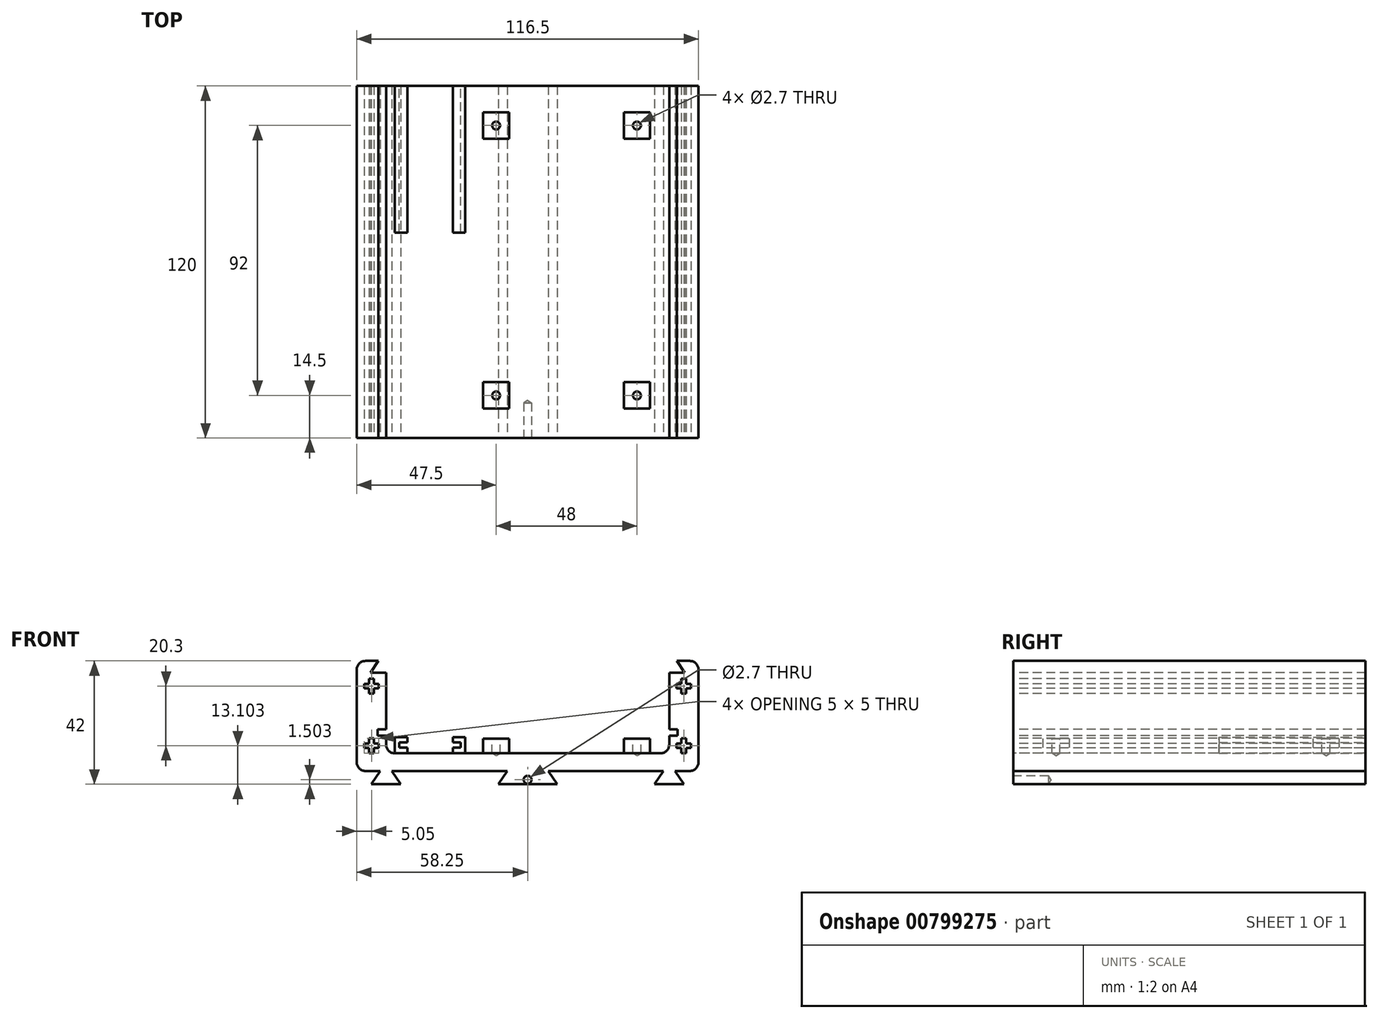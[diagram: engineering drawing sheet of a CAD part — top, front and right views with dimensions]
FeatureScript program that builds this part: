
annotation { "Feature Type Name" : "Feature", "Feature Type Description" : "" }
export const myFeature = defineFeature(function(context is Context, id is Id, definition is map)
    precondition{}
    {
        {
            var Q0;
            Q0=qCreatedBy(makeId("Front.planeOp"),FACE);
            var sketch = newSketch(context, id + "F0", { "sketchPlane" : qUnion([Q0])});
            skLineSegment(sketch, "E0", {"start": v(0, -17) * mm, "end": v(-10.04, -17) * mm});
            skLineSegment(sketch, "E1", {"start": v(-10.04, -17) * mm, "end": v(-7, -12.5) * mm});
            skLineSegment(sketch, "E2", {"start": v(-7, -12.5) * mm, "end": v(-46.25, -12.5) * mm});
            skLineSegment(sketch, "E3", {"start": v(-46.25, -12.5) * mm, "end": v(-43.21, -17) * mm});
            skLineSegment(sketch, "E4", {"start": v(-43.21, -17) * mm, "end": v(-53.29, -17) * mm});
            skLineSegment(sketch, "E5", {"start": v(-53.29, -17) * mm, "end": v(-50.25, -12.5) * mm});
            skLineSegment(sketch, "E6", {"start": v(-50.25, -12.5) * mm, "end": v(-55.25, -12.5) * mm});
            skLineSegment(sketch, "E7", {"start": v(-58.25, -9.5) * mm, "end": v(-58.25, 22) * mm});
            skLineSegment(sketch, "E8", {"start": v(-55.25, 25) * mm, "end": v(-50.87, 25) * mm});
            skLineSegment(sketch, "E9", {"start": v(-50.87, 25) * mm, "end": v(-53.5, 21) * mm});
            skLineSegment(sketch, "E10", {"start": v(-53.5, 21) * mm, "end": v(-48.25, 21) * mm});
            skLineSegment(sketch, "E11", {"start": v(-48.25, 21) * mm, "end": v(-48.25, 1.7) * mm});
            skLineSegment(sketch, "E12", {"start": v(-48.25, 1.7) * mm, "end": v(-51.1, 1.7) * mm});
            skLineSegment(sketch, "E13", {"start": v(-51.1, 1.7) * mm, "end": v(-51.1, -0.5) * mm});
            skLineSegment(sketch, "E14", {"start": v(-51.1, -0.5) * mm, "end": v(-48.25, -0.5) * mm});
            skLineSegment(sketch, "E15", {"start": v(-48.25, -0.5) * mm, "end": v(-48.25, -3.5) * mm});
            skLineSegment(sketch, "E16", {"start": v(-45.25, -6.5) * mm, "end": v(0, -6.5) * mm});
            skLineSegment(sketch, "E17", {"start": v(-48.25, 29.47) * mm, "end": v(-48.25, -26.87) * mm, "construction": true});
            skPoint(sketch, "E18.visualSharp", {"position": v(-58.25, 25) * mm});
            skArc(sketch, "E18.filletArc", {"start": v(-55.25, 25) * mm, "mid": v(-57.37, 24.11) * mm, "end": v(-58.25, 22) * mm});
            skPoint(sketch, "E19.visualSharp", {"position": v(-58.25, -12.5) * mm});
            skArc(sketch, "E19.filletArc", {"start": v(-58.25, -9.5) * mm, "mid": v(-57.37, -11.63) * mm, "end": v(-55.25, -12.5) * mm});
            skPoint(sketch, "E20.visualSharp", {"position": v(-48.25, -6.5) * mm});
            skArc(sketch, "E20.filletArc", {"start": v(-48.25, -3.5) * mm, "mid": v(-47.37, -5.63) * mm, "end": v(-45.25, -6.5) * mm});
            skLineSegment(sketch, "E21", {"start": v(-53.2, 35.2) * mm, "end": v(-53.2, -9.28) * mm, "construction": true});
            skLineSegment(sketch, "E22", {"start": v(-92.18, 6.24) * mm, "end": v(0, 6.24) * mm, "construction": true});
            skArc(sketch, "E23.MirrorCS", {"start": v(48.25, -3.5) * mm, "mid": v(47.37, -5.63) * mm, "end": v(45.25, -6.5) * mm});
            skArc(sketch, "E24.MirrorCS", {"start": v(55.25, 25) * mm, "mid": v(57.37, 24.11) * mm, "end": v(58.25, 22) * mm});
            skLineSegment(sketch, "E25.MirrorCS", {"start": v(48.25, -0.5) * mm, "end": v(48.25, -3.5) * mm});
            skLineSegment(sketch, "E26.MirrorCS", {"start": v(46.25, -12.5) * mm, "end": v(43.21, -17) * mm});
            skLineSegment(sketch, "E27.MirrorCS", {"start": v(51.1, 1.7) * mm, "end": v(51.1, -0.5) * mm});
            skLineSegment(sketch, "E28.MirrorCS", {"start": v(53.29, -17) * mm, "end": v(50.25, -12.5) * mm});
            skLineSegment(sketch, "E29.MirrorCS", {"start": v(10.04, -17) * mm, "end": v(7, -12.5) * mm});
            skLineSegment(sketch, "E30.MirrorCS", {"start": v(48.25, 1.7) * mm, "end": v(51.1, 1.7) * mm});
            skLineSegment(sketch, "E31.MirrorCS", {"start": v(51.1, -0.5) * mm, "end": v(48.25, -0.5) * mm});
            skArc(sketch, "E32.MirrorCS", {"start": v(58.25, -9.5) * mm, "mid": v(57.37, -11.63) * mm, "end": v(55.25, -12.5) * mm});
            skLineSegment(sketch, "E33.MirrorCS", {"start": v(45.25, -6.5) * mm, "end": v(0, -6.5) * mm});
            skLineSegment(sketch, "E34.MirrorCS", {"start": v(48.25, 29.47) * mm, "end": v(48.25, -26.87) * mm, "construction": true});
            skLineSegment(sketch, "E35.MirrorCS", {"start": v(0, -17) * mm, "end": v(10.04, -17) * mm});
            skPoint(sketch, "E36.MirrorP", {"position": v(58.25, -12.5) * mm});
            skLineSegment(sketch, "E37.MirrorCS", {"start": v(7, -12.5) * mm, "end": v(46.25, -12.5) * mm});
            skLineSegment(sketch, "E38.MirrorCS", {"start": v(43.21, -17) * mm, "end": v(53.29, -17) * mm});
            skPoint(sketch, "E39.MirrorP", {"position": v(58.25, 25) * mm});
            skLineSegment(sketch, "E40.MirrorCS", {"start": v(50.25, -12.5) * mm, "end": v(55.25, -12.5) * mm});
            skLineSegment(sketch, "E41.MirrorCS", {"start": v(53.2, 35.2) * mm, "end": v(53.2, -9.28) * mm, "construction": true});
            skPoint(sketch, "E42.MirrorP", {"position": v(48.25, -6.5) * mm});
            skLineSegment(sketch, "E43.MirrorCS", {"start": v(58.25, -9.5) * mm, "end": v(58.25, 22) * mm});
            skLineSegment(sketch, "E44.MirrorCS", {"start": v(53.5, 21) * mm, "end": v(48.25, 21) * mm});
            skLineSegment(sketch, "E45.MirrorCS", {"start": v(48.25, 21) * mm, "end": v(48.25, 1.7) * mm});
            skLineSegment(sketch, "E46.MirrorCS", {"start": v(55.25, 25) * mm, "end": v(50.87, 25) * mm});
            skLineSegment(sketch, "E47.MirrorCS", {"start": v(50.87, 25) * mm, "end": v(53.5, 21) * mm});
            skPoint(sketch, "E48", {"position": v(-53.2, 16.4) * mm});
            skPoint(sketch, "E49", {"position": v(-53.2, -3.9) * mm});
            skLineSegment(sketch, "E50", {"start": v(-55.7, 17.2) * mm, "end": v(-54, 17.2) * mm});
            skLineSegment(sketch, "E51", {"start": v(-54, 17.2) * mm, "end": v(-54, 18.9) * mm});
            skLineSegment(sketch, "E52", {"start": v(-54, 18.9) * mm, "end": v(-52.4, 18.9) * mm});
            skLineSegment(sketch, "E53", {"start": v(-52.4, 18.9) * mm, "end": v(-52.4, 17.2) * mm});
            skLineSegment(sketch, "E54", {"start": v(-52.4, 17.2) * mm, "end": v(-50.7, 17.2) * mm});
            skLineSegment(sketch, "E55", {"start": v(-50.7, 17.2) * mm, "end": v(-50.7, 15.6) * mm});
            skLineSegment(sketch, "E56", {"start": v(-50.7, 15.6) * mm, "end": v(-52.4, 15.6) * mm});
            skLineSegment(sketch, "E57", {"start": v(-52.4, 15.6) * mm, "end": v(-52.4, 13.9) * mm});
            skLineSegment(sketch, "E58", {"start": v(-52.4, 13.9) * mm, "end": v(-54, 13.9) * mm});
            skLineSegment(sketch, "E59", {"start": v(-54, 13.9) * mm, "end": v(-54, 15.6) * mm});
            skLineSegment(sketch, "E60", {"start": v(-54, 15.6) * mm, "end": v(-55.7, 15.6) * mm});
            skLineSegment(sketch, "E61", {"start": v(-55.7, 15.6) * mm, "end": v(-55.7, 17.2) * mm});
            skLineSegment(sketch, "E62", {"start": v(-50.4, 16.4) * mm, "end": v(-59.4, 16.4) * mm, "construction": true});
            skLineSegment(sketch, "E63", {"start": v(-49.34, -3.9) * mm, "end": v(-57.36, -3.9) * mm, "construction": true});
            skLineSegment(sketch, "E64", {"start": v(-54, -1.4) * mm, "end": v(-52.4, -1.4) * mm});
            skLineSegment(sketch, "E65", {"start": v(-52.4, -1.4) * mm, "end": v(-52.4, -3.1) * mm});
            skLineSegment(sketch, "E66", {"start": v(-52.4, -3.1) * mm, "end": v(-50.7, -3.1) * mm});
            skLineSegment(sketch, "E67", {"start": v(-50.7, -3.1) * mm, "end": v(-50.7, -4.7) * mm});
            skLineSegment(sketch, "E68", {"start": v(-50.7, -4.7) * mm, "end": v(-52.4, -4.7) * mm});
            skLineSegment(sketch, "E69", {"start": v(-52.4, -4.7) * mm, "end": v(-52.4, -6.4) * mm});
            skLineSegment(sketch, "E70", {"start": v(-52.4, -6.4) * mm, "end": v(-54, -6.4) * mm});
            skLineSegment(sketch, "E71", {"start": v(-54, -6.4) * mm, "end": v(-54, -4.7) * mm});
            skLineSegment(sketch, "E72", {"start": v(-54, -4.7) * mm, "end": v(-55.7, -4.7) * mm});
            skLineSegment(sketch, "E73", {"start": v(-55.7, -4.7) * mm, "end": v(-55.7, -3.1) * mm});
            skLineSegment(sketch, "E74", {"start": v(-55.7, -3.1) * mm, "end": v(-54, -3.1) * mm});
            skLineSegment(sketch, "E75", {"start": v(-54, -3.1) * mm, "end": v(-54, -1.4) * mm});
            skLineSegment(sketch, "E76.MirrorCS", {"start": v(54, 17.2) * mm, "end": v(54, 18.9) * mm});
            skLineSegment(sketch, "E77.MirrorCS", {"start": v(54, 18.9) * mm, "end": v(52.4, 18.9) * mm});
            skLineSegment(sketch, "E78.MirrorCS", {"start": v(52.4, 18.9) * mm, "end": v(52.4, 17.2) * mm});
            skLineSegment(sketch, "E79.MirrorCS", {"start": v(52.4, 17.2) * mm, "end": v(50.7, 17.2) * mm});
            skLineSegment(sketch, "E80.MirrorCS", {"start": v(50.7, 17.2) * mm, "end": v(50.7, 15.6) * mm});
            skLineSegment(sketch, "E81.MirrorCS", {"start": v(50.7, 15.6) * mm, "end": v(52.4, 15.6) * mm});
            skLineSegment(sketch, "E82.MirrorCS", {"start": v(52.4, 15.6) * mm, "end": v(52.4, 13.9) * mm});
            skLineSegment(sketch, "E83.MirrorCS", {"start": v(52.4, 13.9) * mm, "end": v(54, 13.9) * mm});
            skLineSegment(sketch, "E84.MirrorCS", {"start": v(54, 13.9) * mm, "end": v(54, 15.6) * mm});
            skLineSegment(sketch, "E85.MirrorCS", {"start": v(54, 15.6) * mm, "end": v(55.7, 15.6) * mm});
            skLineSegment(sketch, "E86.MirrorCS", {"start": v(55.7, 15.6) * mm, "end": v(55.7, 17.2) * mm});
            skLineSegment(sketch, "E87.MirrorCS", {"start": v(55.7, 17.2) * mm, "end": v(54, 17.2) * mm});
            skLineSegment(sketch, "E88.MirrorCS", {"start": v(54, -1.4) * mm, "end": v(52.4, -1.4) * mm});
            skLineSegment(sketch, "E89.MirrorCS", {"start": v(52.4, -1.4) * mm, "end": v(52.4, -3.1) * mm});
            skLineSegment(sketch, "E90.MirrorCS", {"start": v(52.4, -3.1) * mm, "end": v(50.7, -3.1) * mm});
            skLineSegment(sketch, "E91.MirrorCS", {"start": v(50.7, -3.1) * mm, "end": v(50.7, -4.7) * mm});
            skLineSegment(sketch, "E92.MirrorCS", {"start": v(50.7, -4.7) * mm, "end": v(52.4, -4.7) * mm});
            skLineSegment(sketch, "E93.MirrorCS", {"start": v(52.4, -4.7) * mm, "end": v(52.4, -6.4) * mm});
            skLineSegment(sketch, "E94.MirrorCS", {"start": v(52.4, -6.4) * mm, "end": v(54, -6.4) * mm});
            skLineSegment(sketch, "E95.MirrorCS", {"start": v(54, -6.4) * mm, "end": v(54, -4.7) * mm});
            skLineSegment(sketch, "E96.MirrorCS", {"start": v(54, -4.7) * mm, "end": v(55.7, -4.7) * mm});
            skLineSegment(sketch, "E97.MirrorCS", {"start": v(55.7, -4.7) * mm, "end": v(55.7, -3.1) * mm});
            skLineSegment(sketch, "E98.MirrorCS", {"start": v(55.7, -3.1) * mm, "end": v(54, -3.1) * mm});
            skLineSegment(sketch, "E99.MirrorCS", {"start": v(54, -3.1) * mm, "end": v(54, -1.4) * mm});
            skSolve(sketch);
        }
        {
            var Q0;
            Q0=qSketchRegion(id+"F0",true);
            extrude(context, id + "F1", {"entities" : qUnion([Q0]), "oppositeDirection" : true, "depth" : 120 * mm, "offsetDistance" : 25 * mm});
        }
        {
            var Q0;
            Q0=makeQuery(id+"F1.opExtrude","CAP_FACE",FACE,{"disambiguationData":[OSD([sQuery(id+"F0.wireOp",EDGE,"E0"),sQuery(id+"F0.wireOp",EDGE,"E1"),sQuery(id+"F0.wireOp",EDGE,"E2"),sQuery(id+"F0.wireOp",EDGE,"E3"),sQuery(id+"F0.wireOp",EDGE,"E4"),sQuery(id+"F0.wireOp",EDGE,"E5"),sQuery(id+"F0.wireOp",EDGE,"E6"),sQuery(id+"F0.wireOp",EDGE,"E7"),sQuery(id+"F0.wireOp",EDGE,"E8"),sQuery(id+"F0.wireOp",EDGE,"E9"),sQuery(id+"F0.wireOp",EDGE,"E10"),sQuery(id+"F0.wireOp",EDGE,"E11"),sQuery(id+"F0.wireOp",EDGE,"E12"),sQuery(id+"F0.wireOp",EDGE,"E13"),sQuery(id+"F0.wireOp",EDGE,"E14"),sQuery(id+"F0.wireOp",EDGE,"E15"),sQuery(id+"F0.wireOp",EDGE,"E16"),sQuery(id+"F0.wireOp",EDGE,"E18.filletArc"),sQuery(id+"F0.wireOp",EDGE,"E19.filletArc"),sQuery(id+"F0.wireOp",EDGE,"E20.filletArc"),sQuery(id+"F0.wireOp",EDGE,"5194898a-ef6c-4157-a49c-2c8236cce61c"),sQuery(id+"F0.wireOp",EDGE,"7f281998-eedb-455a-a055-9dc59b9fbc9e"),sQuery(id+"F0.wireOp",EDGE,"E23.MirrorCS"),sQuery(id+"F0.wireOp",EDGE,"E24.MirrorCS"),sQuery(id+"F0.wireOp",EDGE,"E25.MirrorCS"),sQuery(id+"F0.wireOp",EDGE,"E26.MirrorCS"),sQuery(id+"F0.wireOp",EDGE,"E27.MirrorCS"),sQuery(id+"F0.wireOp",EDGE,"E28.MirrorCS"),sQuery(id+"F0.wireOp",EDGE,"E29.MirrorCS"),sQuery(id+"F0.wireOp",EDGE,"E30.MirrorCS"),sQuery(id+"F0.wireOp",EDGE,"E31.MirrorCS"),sQuery(id+"F0.wireOp",EDGE,"d584a0aa-b8c3-4ab9-8824-3ea712040d109.MirrorC"),sQuery(id+"F0.wireOp",EDGE,"E32.MirrorCS"),sQuery(id+"F0.wireOp",EDGE,"E241.MirrorC"),sQuery(id+"F0.wireOp",EDGE,"E33.MirrorCS"),sQuery(id+"F0.wireOp",EDGE,"E35.MirrorCS"),sQuery(id+"F0.wireOp",EDGE,"E37.MirrorCS"),sQuery(id+"F0.wireOp",EDGE,"E38.MirrorCS"),sQuery(id+"F0.wireOp",EDGE,"E40.MirrorCS"),sQuery(id+"F0.wireOp",EDGE,"E43.MirrorCS"),sQuery(id+"F0.wireOp",EDGE,"E44.MirrorCS"),sQuery(id+"F0.wireOp",EDGE,"E45.MirrorCS"),sQuery(id+"F0.wireOp",EDGE,"E46.MirrorCS"),sQuery(id+"F0.wireOp",EDGE,"E47.MirrorCS")])],"isStart":true});
            var sketch = newSketch(context, id + "F2", { "sketchPlane" : qUnion([Q0])});
            skPoint(sketch, "E100", {"position": v(0, -15.5) * mm});
            skSolve(sketch);
        }
        {
            var Q0;
            Q0=sQuery(id+"F2.wireOp",VERTEX,"E100");
            var Q1;
            Q1=makeQuery(id+"F1.opExtrude","SWEPT_BODY",BODY,{"disambiguationData":[OSD([sQuery(id+"F0.wireOp",EDGE,"E0"),sQuery(id+"F0.wireOp",EDGE,"E1"),sQuery(id+"F0.wireOp",EDGE,"E2"),sQuery(id+"F0.wireOp",EDGE,"E3"),sQuery(id+"F0.wireOp",EDGE,"E4"),sQuery(id+"F0.wireOp",EDGE,"E5"),sQuery(id+"F0.wireOp",EDGE,"E6"),sQuery(id+"F0.wireOp",EDGE,"E7"),sQuery(id+"F0.wireOp",EDGE,"E8"),sQuery(id+"F0.wireOp",EDGE,"E9"),sQuery(id+"F0.wireOp",EDGE,"E10"),sQuery(id+"F0.wireOp",EDGE,"E11"),sQuery(id+"F0.wireOp",EDGE,"E12"),sQuery(id+"F0.wireOp",EDGE,"E13"),sQuery(id+"F0.wireOp",EDGE,"E14"),sQuery(id+"F0.wireOp",EDGE,"E15"),sQuery(id+"F0.wireOp",EDGE,"E16"),sQuery(id+"F0.wireOp",EDGE,"E18.filletArc"),sQuery(id+"F0.wireOp",EDGE,"E19.filletArc"),sQuery(id+"F0.wireOp",EDGE,"E20.filletArc"),sQuery(id+"F0.wireOp",EDGE,"5194898a-ef6c-4157-a49c-2c8236cce61c"),sQuery(id+"F0.wireOp",EDGE,"7f281998-eedb-455a-a055-9dc59b9fbc9e"),sQuery(id+"F0.wireOp",EDGE,"E23.MirrorCS"),sQuery(id+"F0.wireOp",EDGE,"E24.MirrorCS"),sQuery(id+"F0.wireOp",EDGE,"E25.MirrorCS"),sQuery(id+"F0.wireOp",EDGE,"E26.MirrorCS"),sQuery(id+"F0.wireOp",EDGE,"E27.MirrorCS"),sQuery(id+"F0.wireOp",EDGE,"E28.MirrorCS"),sQuery(id+"F0.wireOp",EDGE,"E29.MirrorCS"),sQuery(id+"F0.wireOp",EDGE,"E30.MirrorCS"),sQuery(id+"F0.wireOp",EDGE,"E31.MirrorCS"),sQuery(id+"F0.wireOp",EDGE,"d584a0aa-b8c3-4ab9-8824-3ea712040d109.MirrorC"),sQuery(id+"F0.wireOp",EDGE,"E32.MirrorCS"),sQuery(id+"F0.wireOp",EDGE,"E241.MirrorC"),sQuery(id+"F0.wireOp",EDGE,"E33.MirrorCS"),sQuery(id+"F0.wireOp",EDGE,"E35.MirrorCS"),sQuery(id+"F0.wireOp",EDGE,"E37.MirrorCS"),sQuery(id+"F0.wireOp",EDGE,"E38.MirrorCS"),sQuery(id+"F0.wireOp",EDGE,"E40.MirrorCS"),sQuery(id+"F0.wireOp",EDGE,"E43.MirrorCS"),sQuery(id+"F0.wireOp",EDGE,"E44.MirrorCS"),sQuery(id+"F0.wireOp",EDGE,"E45.MirrorCS"),sQuery(id+"F0.wireOp",EDGE,"E46.MirrorCS"),sQuery(id+"F0.wireOp",EDGE,"E47.MirrorCS")])]});
            hole(context, id + "F3", {"style" : HoleStyle.SIMPLE, "holeDiameter" : 2.7 * mm, "endStyle" : HoleEndStyle.BLIND, "holeDepth" : 12 * mm, "locations" : qUnion([Q0]), "scope" : qUnion([Q1])});
        }
        {
            var Q0;
            Q0=makeQuery(id+"F1.opExtrude","SWEPT_FACE",FACE,{"disambiguationData":[OSD([sQuery(id+"F0.wireOp",EDGE,"E16"),sQuery(id+"F0.wireOp",EDGE,"E33.MirrorCS")])]});
            var sketch = newSketch(context, id + "F4", { "sketchPlane" : qUnion([Q0])});
            skLineSegment(sketch, "E101.bottom", {"start": v(-15.25, 19) * mm, "end": v(-6.25, 19) * mm});
            skLineSegment(sketch, "E101.top", {"start": v(-15.25, 10) * mm, "end": v(-6.25, 10) * mm});
            skLineSegment(sketch, "E101.left", {"start": v(-15.25, 19) * mm, "end": v(-15.25, 10) * mm});
            skLineSegment(sketch, "E101.right", {"start": v(-6.25, 19) * mm, "end": v(-6.25, 10) * mm});
            skLineSegment(sketch, "E102.0.1.0", {"start": v(-6.25, 111) * mm, "end": v(-6.25, 102) * mm});
            skLineSegment(sketch, "E102.0.1.1", {"start": v(-15.25, 111) * mm, "end": v(-15.25, 102) * mm});
            skLineSegment(sketch, "E102.0.1.2", {"start": v(-15.25, 102) * mm, "end": v(-6.25, 102) * mm});
            skLineSegment(sketch, "E102.0.1.3", {"start": v(-15.25, 111) * mm, "end": v(-6.25, 111) * mm});
            skLineSegment(sketch, "E102.1.0.0", {"start": v(41.75, 19) * mm, "end": v(41.75, 10) * mm});
            skLineSegment(sketch, "E102.1.0.1", {"start": v(32.75, 19) * mm, "end": v(32.75, 10) * mm});
            skLineSegment(sketch, "E102.1.0.2", {"start": v(32.75, 10) * mm, "end": v(41.75, 10) * mm});
            skLineSegment(sketch, "E102.1.0.3", {"start": v(32.75, 19) * mm, "end": v(41.75, 19) * mm});
            skLineSegment(sketch, "E102.1.1.0", {"start": v(41.75, 111) * mm, "end": v(41.75, 102) * mm});
            skLineSegment(sketch, "E102.1.1.1", {"start": v(32.75, 111) * mm, "end": v(32.75, 102) * mm});
            skLineSegment(sketch, "E102.1.1.2", {"start": v(32.75, 102) * mm, "end": v(41.75, 102) * mm});
            skLineSegment(sketch, "E102.1.1.3", {"start": v(32.75, 111) * mm, "end": v(41.75, 111) * mm});
            skLineSegment(sketch, "E102.direction1", {"start": v(-15.25, 10) * mm, "end": v(32.75, 10) * mm, "construction": true});
            skLineSegment(sketch, "E102.direction2", {"start": v(-15.25, 10) * mm, "end": v(-15.25, 102) * mm, "construction": true});
            skSolve(sketch);
        }
        {
            var Q0;
            Q0 = qSketchRegion(id + "F4", true);
            extrude(context, id + "F5", {"entities" : qUnion([Q0]), "operationType" : NewBodyOperationType.ADD, "depth" : 5 * mm, "offsetDistance" : 25 * mm});
        }
        {
            var Q0;
            Q0=makeQuery(id+"F5.opExtrude","CAP_FACE",FACE,{"disambiguationData":[OSD([sQuery(id+"F4.wireOp",EDGE,"E102.0.1.0"),sQuery(id+"F4.wireOp",EDGE,"E102.0.1.1"),sQuery(id+"F4.wireOp",EDGE,"E102.0.1.2"),sQuery(id+"F4.wireOp",EDGE,"E102.0.1.3")])],"isStart":false});
            var sketch = newSketch(context, id + "F6", { "sketchPlane" : qUnion([Q0])});
            skPoint(sketch, "E103", {"position": v(-10.75, 106.5) * mm});
            skPoint(sketch, "E103.positionSnap0", {"position": v(-10.75, 111) * mm});
            skPoint(sketch, "E103.positionSnap1", {"position": v(-6.25, 106.5) * mm});
            skPoint(sketch, "E104.0.1.0", {"position": v(-10.75, 14.5) * mm});
            skPoint(sketch, "E104.1.0.0", {"position": v(37.25, 106.5) * mm});
            skPoint(sketch, "E104.1.1.0", {"position": v(37.25, 14.5) * mm});
            skLineSegment(sketch, "E104.direction1", {"start": v(-10.75, 106.5) * mm, "end": v(37.25, 106.5) * mm, "construction": true});
            skLineSegment(sketch, "E104.direction2", {"start": v(-10.75, 106.5) * mm, "end": v(-10.75, 14.5) * mm, "construction": true});
            skSolve(sketch);
        }
        {
            var Q0;
            Q0=sQuery(id+"F6.wireOp",VERTEX,"E103");
            var Q1;
            Q1=sQuery(id+"F6.wireOp",VERTEX,"E104.1.0.0");
            var Q2;
            Q2=sQuery(id+"F6.wireOp",VERTEX,"E104.0.1.0");
            var Q3;
            Q3=sQuery(id+"F6.wireOp",VERTEX,"E104.1.1.0");
            var Q4;
            Q4=makeQuery(id+"F1.opExtrude","SWEPT_BODY",BODY,{"disambiguationData":[OSD([sQuery(id+"F0.wireOp",EDGE,"E0"),sQuery(id+"F0.wireOp",EDGE,"E1"),sQuery(id+"F0.wireOp",EDGE,"E2"),sQuery(id+"F0.wireOp",EDGE,"E3"),sQuery(id+"F0.wireOp",EDGE,"E4"),sQuery(id+"F0.wireOp",EDGE,"E5"),sQuery(id+"F0.wireOp",EDGE,"E6"),sQuery(id+"F0.wireOp",EDGE,"E7"),sQuery(id+"F0.wireOp",EDGE,"E8"),sQuery(id+"F0.wireOp",EDGE,"E9"),sQuery(id+"F0.wireOp",EDGE,"E10"),sQuery(id+"F0.wireOp",EDGE,"E11"),sQuery(id+"F0.wireOp",EDGE,"E12"),sQuery(id+"F0.wireOp",EDGE,"E13"),sQuery(id+"F0.wireOp",EDGE,"E14"),sQuery(id+"F0.wireOp",EDGE,"E15"),sQuery(id+"F0.wireOp",EDGE,"E16"),sQuery(id+"F0.wireOp",EDGE,"E18.filletArc"),sQuery(id+"F0.wireOp",EDGE,"E19.filletArc"),sQuery(id+"F0.wireOp",EDGE,"E20.filletArc"),sQuery(id+"F0.wireOp",EDGE,"E23.MirrorCS"),sQuery(id+"F0.wireOp",EDGE,"E24.MirrorCS"),sQuery(id+"F0.wireOp",EDGE,"E25.MirrorCS"),sQuery(id+"F0.wireOp",EDGE,"E26.MirrorCS"),sQuery(id+"F0.wireOp",EDGE,"E27.MirrorCS"),sQuery(id+"F0.wireOp",EDGE,"E28.MirrorCS"),sQuery(id+"F0.wireOp",EDGE,"E29.MirrorCS"),sQuery(id+"F0.wireOp",EDGE,"E30.MirrorCS"),sQuery(id+"F0.wireOp",EDGE,"E31.MirrorCS"),sQuery(id+"F0.wireOp",EDGE,"E32.MirrorCS"),sQuery(id+"F0.wireOp",EDGE,"E33.MirrorCS"),sQuery(id+"F0.wireOp",EDGE,"E35.MirrorCS"),sQuery(id+"F0.wireOp",EDGE,"E37.MirrorCS"),sQuery(id+"F0.wireOp",EDGE,"E38.MirrorCS"),sQuery(id+"F0.wireOp",EDGE,"E40.MirrorCS"),sQuery(id+"F0.wireOp",EDGE,"E43.MirrorCS"),sQuery(id+"F0.wireOp",EDGE,"E44.MirrorCS"),sQuery(id+"F0.wireOp",EDGE,"E45.MirrorCS"),sQuery(id+"F0.wireOp",EDGE,"E46.MirrorCS"),sQuery(id+"F0.wireOp",EDGE,"E47.MirrorCS"),sQuery(id+"F0.wireOp",EDGE,"E50"),sQuery(id+"F0.wireOp",EDGE,"E51"),sQuery(id+"F0.wireOp",EDGE,"E52"),sQuery(id+"F0.wireOp",EDGE,"E53"),sQuery(id+"F0.wireOp",EDGE,"E54"),sQuery(id+"F0.wireOp",EDGE,"E55"),sQuery(id+"F0.wireOp",EDGE,"E56"),sQuery(id+"F0.wireOp",EDGE,"E57"),sQuery(id+"F0.wireOp",EDGE,"E58"),sQuery(id+"F0.wireOp",EDGE,"E59"),sQuery(id+"F0.wireOp",EDGE,"E60"),sQuery(id+"F0.wireOp",EDGE,"E61"),sQuery(id+"F0.wireOp",EDGE,"E64"),sQuery(id+"F0.wireOp",EDGE,"E65"),sQuery(id+"F0.wireOp",EDGE,"E66"),sQuery(id+"F0.wireOp",EDGE,"E67"),sQuery(id+"F0.wireOp",EDGE,"E68"),sQuery(id+"F0.wireOp",EDGE,"E69"),sQuery(id+"F0.wireOp",EDGE,"E70"),sQuery(id+"F0.wireOp",EDGE,"E71"),sQuery(id+"F0.wireOp",EDGE,"E72"),sQuery(id+"F0.wireOp",EDGE,"E73"),sQuery(id+"F0.wireOp",EDGE,"E74"),sQuery(id+"F0.wireOp",EDGE,"E75"),sQuery(id+"F0.wireOp",EDGE,"E76.MirrorCS"),sQuery(id+"F0.wireOp",EDGE,"E77.MirrorCS"),sQuery(id+"F0.wireOp",EDGE,"E78.MirrorCS"),sQuery(id+"F0.wireOp",EDGE,"E79.MirrorCS"),sQuery(id+"F0.wireOp",EDGE,"E80.MirrorCS"),sQuery(id+"F0.wireOp",EDGE,"E81.MirrorCS"),sQuery(id+"F0.wireOp",EDGE,"E82.MirrorCS"),sQuery(id+"F0.wireOp",EDGE,"E83.MirrorCS"),sQuery(id+"F0.wireOp",EDGE,"E84.MirrorCS"),sQuery(id+"F0.wireOp",EDGE,"E85.MirrorCS"),sQuery(id+"F0.wireOp",EDGE,"E86.MirrorCS"),sQuery(id+"F0.wireOp",EDGE,"E87.MirrorCS"),sQuery(id+"F0.wireOp",EDGE,"E88.MirrorCS"),sQuery(id+"F0.wireOp",EDGE,"E89.MirrorCS"),sQuery(id+"F0.wireOp",EDGE,"E90.MirrorCS"),sQuery(id+"F0.wireOp",EDGE,"E91.MirrorCS"),sQuery(id+"F0.wireOp",EDGE,"E92.MirrorCS"),sQuery(id+"F0.wireOp",EDGE,"E93.MirrorCS"),sQuery(id+"F0.wireOp",EDGE,"E94.MirrorCS"),sQuery(id+"F0.wireOp",EDGE,"E95.MirrorCS"),sQuery(id+"F0.wireOp",EDGE,"E96.MirrorCS"),sQuery(id+"F0.wireOp",EDGE,"E97.MirrorCS"),sQuery(id+"F0.wireOp",EDGE,"E98.MirrorCS"),sQuery(id+"F0.wireOp",EDGE,"E99.MirrorCS")])]});
            hole(context, id + "F7", {"style" : HoleStyle.SIMPLE, "endStyle" : HoleEndStyle.BLIND, "holeDiameter" : 2.7 * mm, "majorDiameter" : 5 * mm, "holeDepth" : 5 * mm, "isTappedThrough" : true, "tappedDepth" : 12 * mm, "tapClearance" : 3, "startFromSketch" : true, "locations" : qUnion([Q0, Q1, Q2, Q3]), "scope" : qUnion([Q4])});
        }
        {
            var Q0;
            Q0=makeQuery(id+"F1.opExtrude","CAP_FACE",FACE,{"disambiguationData":[OSD([sQuery(id+"F0.wireOp",EDGE,"E0"),sQuery(id+"F0.wireOp",EDGE,"E1"),sQuery(id+"F0.wireOp",EDGE,"E2"),sQuery(id+"F0.wireOp",EDGE,"E3"),sQuery(id+"F0.wireOp",EDGE,"E4"),sQuery(id+"F0.wireOp",EDGE,"E5"),sQuery(id+"F0.wireOp",EDGE,"E6"),sQuery(id+"F0.wireOp",EDGE,"E7"),sQuery(id+"F0.wireOp",EDGE,"E8"),sQuery(id+"F0.wireOp",EDGE,"E9"),sQuery(id+"F0.wireOp",EDGE,"E10"),sQuery(id+"F0.wireOp",EDGE,"E11"),sQuery(id+"F0.wireOp",EDGE,"E12"),sQuery(id+"F0.wireOp",EDGE,"E13"),sQuery(id+"F0.wireOp",EDGE,"E14"),sQuery(id+"F0.wireOp",EDGE,"E15"),sQuery(id+"F0.wireOp",EDGE,"E16"),sQuery(id+"F0.wireOp",EDGE,"E18.filletArc"),sQuery(id+"F0.wireOp",EDGE,"E19.filletArc"),sQuery(id+"F0.wireOp",EDGE,"E20.filletArc"),sQuery(id+"F0.wireOp",EDGE,"E23.MirrorCS"),sQuery(id+"F0.wireOp",EDGE,"E24.MirrorCS"),sQuery(id+"F0.wireOp",EDGE,"E25.MirrorCS"),sQuery(id+"F0.wireOp",EDGE,"E26.MirrorCS"),sQuery(id+"F0.wireOp",EDGE,"E27.MirrorCS"),sQuery(id+"F0.wireOp",EDGE,"E28.MirrorCS"),sQuery(id+"F0.wireOp",EDGE,"E29.MirrorCS"),sQuery(id+"F0.wireOp",EDGE,"E30.MirrorCS"),sQuery(id+"F0.wireOp",EDGE,"E31.MirrorCS"),sQuery(id+"F0.wireOp",EDGE,"E32.MirrorCS"),sQuery(id+"F0.wireOp",EDGE,"E33.MirrorCS"),sQuery(id+"F0.wireOp",EDGE,"E35.MirrorCS"),sQuery(id+"F0.wireOp",EDGE,"E37.MirrorCS"),sQuery(id+"F0.wireOp",EDGE,"E38.MirrorCS"),sQuery(id+"F0.wireOp",EDGE,"E40.MirrorCS"),sQuery(id+"F0.wireOp",EDGE,"E43.MirrorCS"),sQuery(id+"F0.wireOp",EDGE,"E44.MirrorCS"),sQuery(id+"F0.wireOp",EDGE,"E45.MirrorCS"),sQuery(id+"F0.wireOp",EDGE,"E46.MirrorCS"),sQuery(id+"F0.wireOp",EDGE,"E47.MirrorCS"),sQuery(id+"F0.wireOp",EDGE,"E50"),sQuery(id+"F0.wireOp",EDGE,"E51"),sQuery(id+"F0.wireOp",EDGE,"E52"),sQuery(id+"F0.wireOp",EDGE,"E53"),sQuery(id+"F0.wireOp",EDGE,"E54"),sQuery(id+"F0.wireOp",EDGE,"E55"),sQuery(id+"F0.wireOp",EDGE,"E56"),sQuery(id+"F0.wireOp",EDGE,"E57"),sQuery(id+"F0.wireOp",EDGE,"E58"),sQuery(id+"F0.wireOp",EDGE,"E59"),sQuery(id+"F0.wireOp",EDGE,"E60"),sQuery(id+"F0.wireOp",EDGE,"E61"),sQuery(id+"F0.wireOp",EDGE,"E64"),sQuery(id+"F0.wireOp",EDGE,"E65"),sQuery(id+"F0.wireOp",EDGE,"E66"),sQuery(id+"F0.wireOp",EDGE,"E67"),sQuery(id+"F0.wireOp",EDGE,"E68"),sQuery(id+"F0.wireOp",EDGE,"E69"),sQuery(id+"F0.wireOp",EDGE,"E70"),sQuery(id+"F0.wireOp",EDGE,"E71"),sQuery(id+"F0.wireOp",EDGE,"E72"),sQuery(id+"F0.wireOp",EDGE,"E73"),sQuery(id+"F0.wireOp",EDGE,"E74"),sQuery(id+"F0.wireOp",EDGE,"E75"),sQuery(id+"F0.wireOp",EDGE,"E76.MirrorCS"),sQuery(id+"F0.wireOp",EDGE,"E77.MirrorCS"),sQuery(id+"F0.wireOp",EDGE,"E78.MirrorCS"),sQuery(id+"F0.wireOp",EDGE,"E79.MirrorCS"),sQuery(id+"F0.wireOp",EDGE,"E80.MirrorCS"),sQuery(id+"F0.wireOp",EDGE,"E81.MirrorCS"),sQuery(id+"F0.wireOp",EDGE,"E82.MirrorCS"),sQuery(id+"F0.wireOp",EDGE,"E83.MirrorCS"),sQuery(id+"F0.wireOp",EDGE,"E84.MirrorCS"),sQuery(id+"F0.wireOp",EDGE,"E85.MirrorCS"),sQuery(id+"F0.wireOp",EDGE,"E86.MirrorCS"),sQuery(id+"F0.wireOp",EDGE,"E87.MirrorCS"),sQuery(id+"F0.wireOp",EDGE,"E88.MirrorCS"),sQuery(id+"F0.wireOp",EDGE,"E89.MirrorCS"),sQuery(id+"F0.wireOp",EDGE,"E90.MirrorCS"),sQuery(id+"F0.wireOp",EDGE,"E91.MirrorCS"),sQuery(id+"F0.wireOp",EDGE,"E92.MirrorCS"),sQuery(id+"F0.wireOp",EDGE,"E93.MirrorCS"),sQuery(id+"F0.wireOp",EDGE,"E94.MirrorCS"),sQuery(id+"F0.wireOp",EDGE,"E95.MirrorCS"),sQuery(id+"F0.wireOp",EDGE,"E96.MirrorCS"),sQuery(id+"F0.wireOp",EDGE,"E97.MirrorCS"),sQuery(id+"F0.wireOp",EDGE,"E98.MirrorCS"),sQuery(id+"F0.wireOp",EDGE,"E99.MirrorCS")])],"isStart":false});
            var sketch = newSketch(context, id + "F8", { "sketchPlane" : qUnion([Q0])});
            skLineSegment(sketch, "E105", {"start": v(21.25, -6.5) * mm, "end": v(21.25, -1) * mm});
            skLineSegment(sketch, "E106", {"start": v(21.25, -1) * mm, "end": v(25.5, -1) * mm});
            skLineSegment(sketch, "E107", {"start": v(25.5, -1) * mm, "end": v(25.5, -2.7) * mm});
            skLineSegment(sketch, "E108", {"start": v(25.5, -2.7) * mm, "end": v(22.75, -2.7) * mm});
            skLineSegment(sketch, "E109", {"start": v(33.25, -8.75) * mm, "end": v(33.25, 2.77) * mm, "construction": true});
            skLineSegment(sketch, "E110", {"start": v(22.75, -2.7) * mm, "end": v(22.75, -4.5) * mm});
            skLineSegment(sketch, "E111", {"start": v(22.75, -4.5) * mm, "end": v(25.5, -4.5) * mm});
            skLineSegment(sketch, "E112", {"start": v(25.5, -4.5) * mm, "end": v(25.5, -6.5) * mm});
            skLineSegment(sketch, "E113.MirrorCS", {"start": v(45.25, -1) * mm, "end": v(41, -1) * mm});
            skLineSegment(sketch, "E114.MirrorCS", {"start": v(45.25, -6.5) * mm, "end": v(45.25, -1) * mm});
            skLineSegment(sketch, "E115.MirrorCS", {"start": v(41, -1) * mm, "end": v(41, -2.7) * mm});
            skLineSegment(sketch, "E116.MirrorCS", {"start": v(41, -4.5) * mm, "end": v(41, -6.5) * mm});
            skLineSegment(sketch, "E117.MirrorCS", {"start": v(43.75, -4.5) * mm, "end": v(41, -4.5) * mm});
            skLineSegment(sketch, "E118.MirrorCS", {"start": v(41, -2.7) * mm, "end": v(43.75, -2.7) * mm});
            skLineSegment(sketch, "E119.MirrorCS", {"start": v(43.75, -2.7) * mm, "end": v(43.75, -4.5) * mm});
            skSolve(sketch);
        }
        {
            var Q0;
            {var subQ0=sQuery(id+"F8.wireOp",EDGE,"E105");Q0=makeQuery(id+"F8.imprint","IMPRINT",FACE,{"disambiguationData":[TD([[makeQuery(id+"F8.imprint","IMPRINT",EDGE,{"derivedFrom":subQ0}),-1.0]])]});}
            var Q1;
            Q1=makeQuery(id+"F8.imprint","IMPRINT",FACE,{"disambiguationData":[TD([[makeQuery(id+"F8.imprint","IMPRINT",EDGE,{"derivedFrom":sQuery(id+"F8.wireOp",EDGE,"E113.MirrorCS")}),1.0]])]});
            extrude(context, id + "F9", {"entities" : qUnion([Q0, Q1]), "operationType" : NewBodyOperationType.ADD, "oppositeDirection" : true, "depth" : 50 * mm, "offsetDistance" : 25 * mm});
        }
    });
